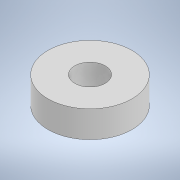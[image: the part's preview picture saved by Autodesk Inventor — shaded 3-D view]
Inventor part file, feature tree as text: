
AUTODESK INVENTOR PART (.ipt)
format: ipt  version: 2022 (Build 260153000, 153)  size: 95,744 bytes
history: native  units: mm
features: extrude x1, sketch x1
ambient origin geometry x8: Origin, YZ Plane, XZ Plane, XY Plane, X Axis, Y Axis, Z Axis, Center Point
bodies: Solid1 (feature_tree)
feature tree (2):
  extrude  "Extrusion1"  Depth=7.0mm
  sketch  "Sketch1"  dims[d0=8.0mm d1=22.0mm d2=7.0mm d3=0.0mm]
